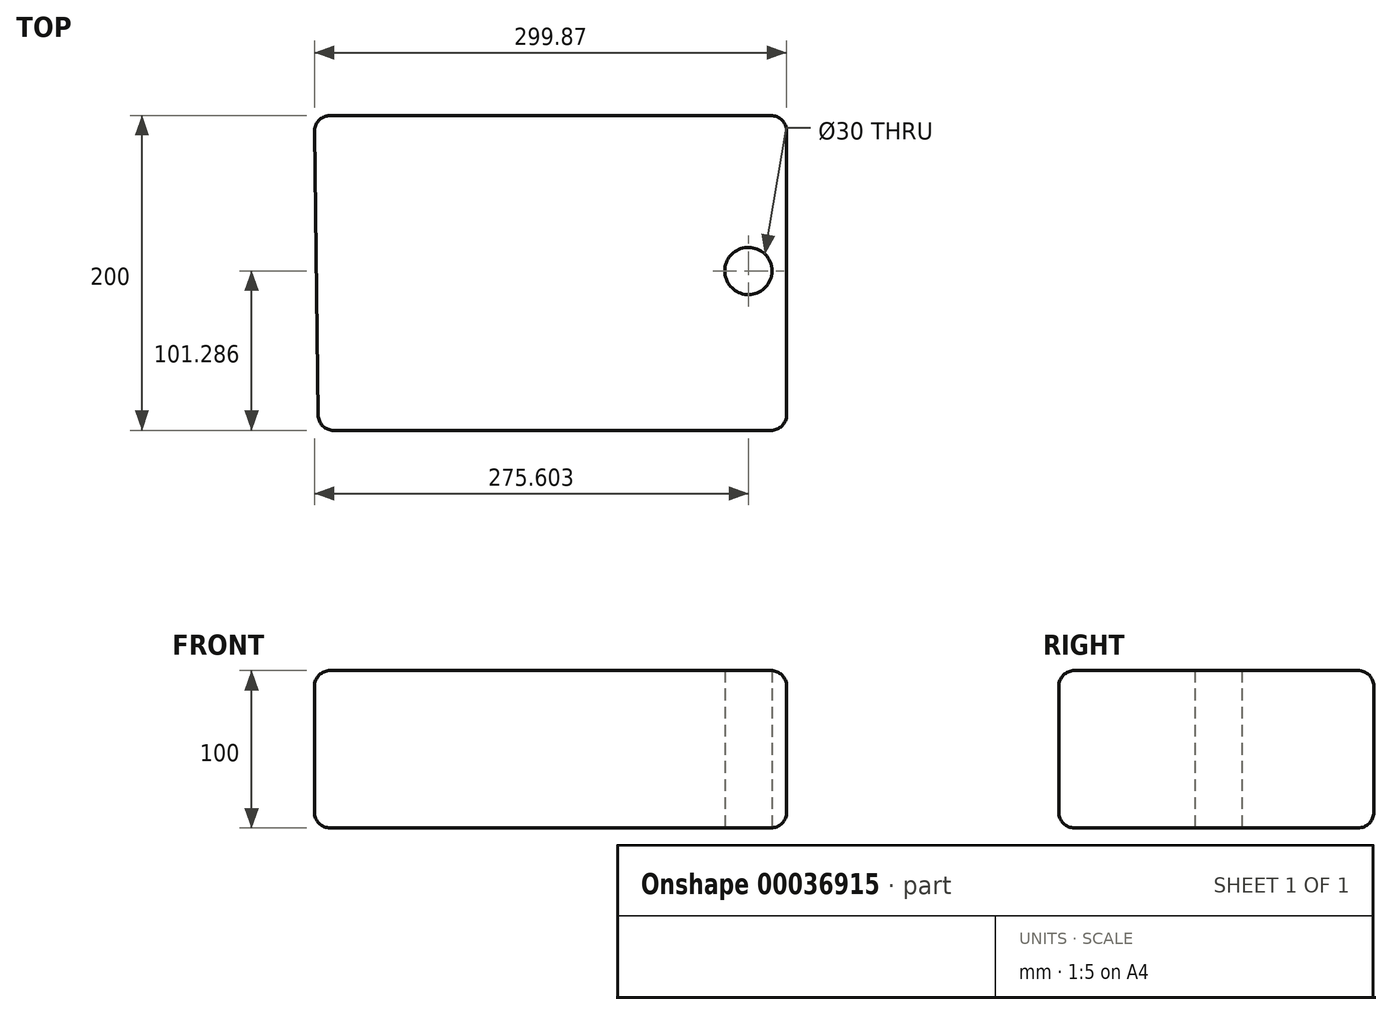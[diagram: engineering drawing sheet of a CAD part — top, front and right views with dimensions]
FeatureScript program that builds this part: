
annotation { "Feature Type Name" : "Feature", "Feature Type Description" : "" }
export const myFeature = defineFeature(function(context is Context, id is Id, definition is map)
    precondition{}
    {
        {
            var Q0;
            Q0=qCreatedBy(makeId("Top.planeOp"),FACE);
            var Q1;
            Q1=qCreatedBy(makeId("Top.planeOp"),FACE);
            var sketch = newSketch(context, id + "F0", { "sketchPlane" : qUnion([Q0, Q1])});
            skLineSegment(sketch, "E0", {"start": v(-151.39, 151.7) * mm, "end": v(148.61, 151.7) * mm});
            skLineSegment(sketch, "E1", {"start": v(148.61, 151.7) * mm, "end": v(148.61, -48.3) * mm});
            skLineSegment(sketch, "E2", {"start": v(148.61, -48.3) * mm, "end": v(-148.84, -48.3) * mm});
            skLineSegment(sketch, "E3", {"start": v(-148.84, -48.3) * mm, "end": v(-151.39, 151.7) * mm});
            skCircle(sketch, "E4", {"center": v(124.34, 52.99) * mm, "radius": 15 * mm});
            skSolve(sketch);
        }
        {
            var Q0;
            Q0=makeQuery(id+"F0.imprint","IMPRINT",FACE,{"disambiguationData":[TD([[makeQuery(id+"F0.imprint","IMPRINT",EDGE,{"derivedFrom":sQuery(id+"F0.wireOp",EDGE,"E0")}),-1.0]])]});
            extrude(context, id + "F1", {"entities" : qUnion([Q0]), "depth" : 100 * mm});
        }
        {
            var Q0;
            Q0=makeQuery(id+"F1.opExtrude","CAP_EDGE",EDGE,{"disambiguationData":[OSD([sQuery(id+"F0.wireOp",EDGE,"E1")])],"isStart":false});
            var Q1;
            Q1=makeQuery(id+"F1.opExtrude","CAP_EDGE",EDGE,{"disambiguationData":[OSD([sQuery(id+"F0.wireOp",EDGE,"E2")])],"isStart":false});
            var Q2;
            Q2=makeQuery(id+"F1.opExtrude","SWEPT_EDGE",EDGE,{"disambiguationData":[OSD([sQuery(id+"F0.wireOp",EDGE,"E1"),sQuery(id+"F0.wireOp",EDGE,"E2")])]});
            var Q3;
            Q3=makeQuery(id+"F1.opExtrude","CAP_EDGE",EDGE,{"disambiguationData":[OSD([sQuery(id+"F0.wireOp",EDGE,"E2")])],"isStart":true});
            var Q4;
            Q4=makeQuery(id+"F1.opExtrude","CAP_EDGE",EDGE,{"disambiguationData":[OSD([sQuery(id+"F0.wireOp",EDGE,"E1")])],"isStart":true});
            var Q5;
            Q5=makeQuery(id+"F1.opExtrude","SWEPT_EDGE",EDGE,{"disambiguationData":[OSD([sQuery(id+"F0.wireOp",EDGE,"E0"),sQuery(id+"F0.wireOp",EDGE,"E1")])]});
            var Q6;
            Q6=makeQuery(id+"F1.opExtrude","CAP_EDGE",EDGE,{"disambiguationData":[OSD([sQuery(id+"F0.wireOp",EDGE,"E0")])],"isStart":true});
            var Q7;
            Q7=makeQuery(id+"F1.opExtrude","CAP_EDGE",EDGE,{"disambiguationData":[OSD([sQuery(id+"F0.wireOp",EDGE,"E3")])],"isStart":true});
            var Q8;
            Q8=makeQuery(id+"F1.opExtrude","CAP_EDGE",EDGE,{"disambiguationData":[OSD([sQuery(id+"F0.wireOp",EDGE,"E3")])],"isStart":false});
            var Q9;
            Q9=makeQuery(id+"F1.opExtrude","SWEPT_EDGE",EDGE,{"disambiguationData":[OSD([sQuery(id+"F0.wireOp",EDGE,"E2"),sQuery(id+"F0.wireOp",EDGE,"E3")])]});
            var Q10;
            Q10=makeQuery(id+"F1.opExtrude","SWEPT_EDGE",EDGE,{"disambiguationData":[OSD([sQuery(id+"F0.wireOp",EDGE,"E0"),sQuery(id+"F0.wireOp",EDGE,"E3")])]});
            var Q11;
            Q11=makeQuery(id+"F1.opExtrude","CAP_EDGE",EDGE,{"disambiguationData":[OSD([sQuery(id+"F0.wireOp",EDGE,"E0")])],"isStart":false});
            fillet(context, id + "F2", {"entities" : qUnion([Q0, Q1, Q2, Q3, Q4, Q5, Q6, Q7, Q8, Q9, Q10, Q11]), "radius" : 10 * mm, "tangentPropagation" : true, "allowEdgeOverflow" : false});
        }
    });
